# Revit family: Haworth_Belong_Tile
name_source: partatom
category: Furniture Systems
revit_build: Autodesk Revit 2018 (Build: 20170223_1515(x64)
units: mm (PartAtom-declared; Revit-internal decimal feet)

## family parameters
Always vertical = Yes
Cut with Voids When Loaded = No
OmniClass Number = 23.40.70.14.64.21
OmniClass Title = Systems Furniture
Part Type = Normal
Room Calculation Point = No
Round Connector Dimension = Use Diameter
Shared = No
Work Plane-Based = No

## types (10) — shared parameters
Actual Depth = 11/16"
Assembly Code = E2020200
Description = Haworth - Belong - Tile
Manufacturer = Haworth
Max. Width = 48"
Min. Width = 18"
Model = Haworth - Belong - Tile
Product Page URL = http://www.haworth.com
Revision Number = 2
Screen Finish = Haworth _ Paint _ Graphite
Size = Verify Final Dim. w/ Haworth
Slat Gap = 1 169/256"
Slat Height = 87/256"
Slat Offset = 1 7/32"
Slat Top Offset = 1 53/64"
Standard Heights = 8, 12 in.
Sustainability Info = https://www.haworth.com
URL = www.haworth.com
Warranty = http://www.haworth.com

## per-type parameters (varying)
| type | 12in Tile Height | 8in Tile Height | Actual Height | Actual Width | Custom Size | Standard 12in | Standard 8in | Standard Widths | Width |
| 8h 24w | No | Yes | 7 7/8" | 24" | No | No | Yes | 24, 30, 36, 42, 48 in. | 24" |
| 8h 30w | No | Yes | 7 7/8" | 30" | No | No | Yes | 24, 30, 36, 42, 48 in. | 30" |
| 8h 36w | No | Yes | 7 7/8" | 36" | No | No | Yes | 24, 30, 36, 42, 48 in. | 36" |
| 8h 42w | No | Yes | 7 7/8" | 42" | No | No | Yes | 24, 30, 36, 42, 48 in. | 42" |
| 8h 48w | No | Yes | 7 7/8" | 48" | No | No | Yes | 24, 30, 36, 42, 48 in. | 48" |
| 12h 18w | Yes | No | 12" | 18" | No | Yes | No | 18, 22, 27, 32, 36 in. | 18" |
| 12h 22w | Yes | No | 12" | 22" | No | Yes | No | 18, 22, 27, 32, 36 in. | 22" |
| 12h 27w | Yes | No | 12" | 27" | No | Yes | No | 18, 22, 27, 32, 36 in. | 27" |
| 12h 32w | Yes | No | 12" | 32" | Yes | No | No | 18, 22, 27, 32, 36 in. | 32" |
| 12h 36w | Yes | No | 12" | 26" | Yes | No | No | 18, 22, 27, 32, 36 in. | 26" |

## geometry (parser evidence)
native form markers: Sweep x3
no freeform markers — native parametric forms only
